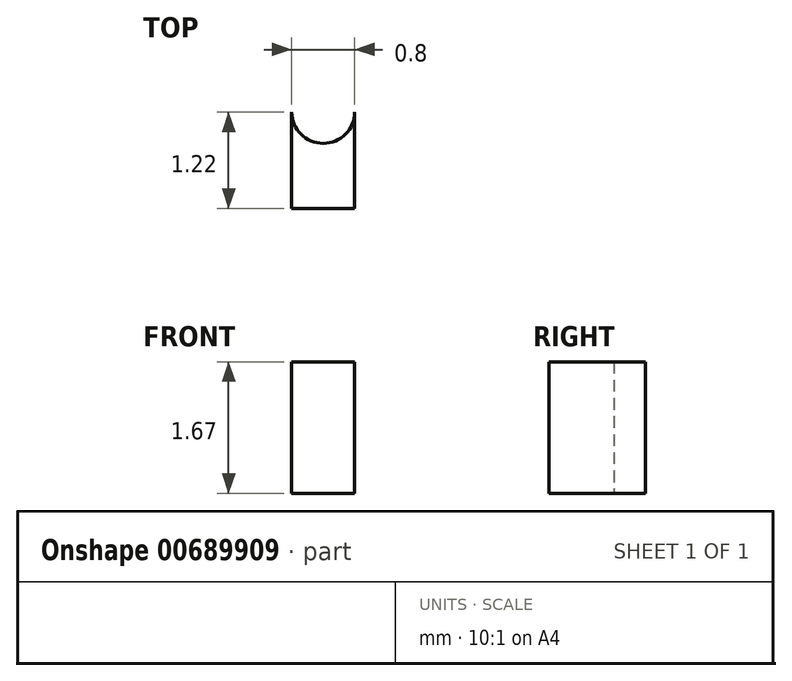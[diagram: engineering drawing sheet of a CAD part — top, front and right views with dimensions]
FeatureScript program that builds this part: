
annotation { "Feature Type Name" : "Feature", "Feature Type Description" : "" }
export const myFeature = defineFeature(function(context is Context, id is Id, definition is map)
    precondition{}
    {
        {
            var Q0;
            Q0=qCreatedBy(makeId("Top.planeOp"),FACE);
            var sketch = newSketch(context, id + "F0", { "sketchPlane" : qUnion([Q0])});
            skLineSegment(sketch, "E0.bottom", {"start": v(0.4, -0.61) * mm, "end": v(-0.4, -0.61) * mm});
            skLineSegment(sketch, "E0.top", {"start": v(0.4, 0.61) * mm, "end": v(-0.4, 0.61) * mm, "construction": true});
            skLineSegment(sketch, "E0.left", {"start": v(0.4, -0.61) * mm, "end": v(0.4, 0.62) * mm});
            skLineSegment(sketch, "E0.right", {"start": v(-0.4, -0.61) * mm, "end": v(-0.4, 0.62) * mm});
            skPoint(sketch, "E0.middle", {"position": v(0, 0) * mm});
            skArc(sketch, "E1", {"start": v(-0.4, 0.61) * mm, "mid": v(0, 0.21) * mm, "end": v(0.4, 0.61) * mm});
            skSolve(sketch);
        }
        {
            var Q0;
            Q0 = qSketchRegion(id + "F0", true);
            extrude(context, id + "F1", {"entities" : qUnion([Q0]), "depth" : (1.6 + 70e-3) * mm, "offsetDistance" : 25 * mm});
        }
    });
